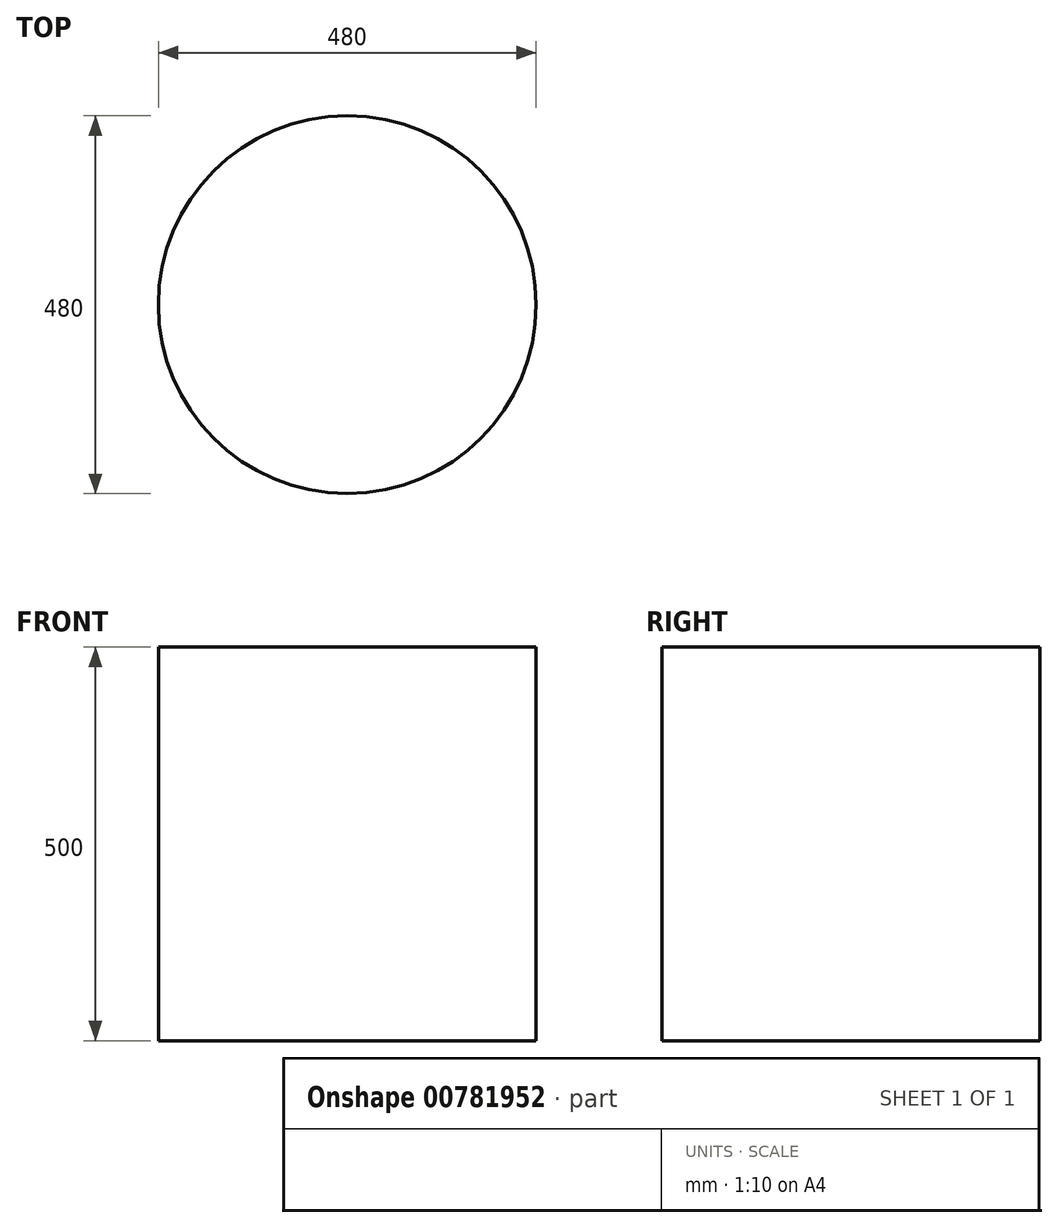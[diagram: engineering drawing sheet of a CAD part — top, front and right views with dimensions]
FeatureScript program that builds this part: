
annotation { "Feature Type Name" : "Feature", "Feature Type Description" : "" }
export const myFeature = defineFeature(function(context is Context, id is Id, definition is map)
    precondition{}
    {
        {
            var Q0;
            Q0=qCreatedBy(makeId("Front.planeOp"),FACE);
            var sketch = newSketch(context, id + "F0", { "sketchPlane" : qUnion([Q0])});
            skLineSegment(sketch, "E0.bottom", {"start": v(0, 479.95) * mm, "end": v(240, 479.95) * mm});
            skLineSegment(sketch, "E0.top", {"start": v(0, -20.05) * mm, "end": v(240, -20.05) * mm});
            skLineSegment(sketch, "E0.left", {"start": v(0, 479.95) * mm, "end": v(0, -20.05) * mm});
            skLineSegment(sketch, "E0.right", {"start": v(240, 479.95) * mm, "end": v(240, -20.05) * mm});
            skSolve(sketch);
        }
        {
            var Q0;
            Q0=makeQuery(id+"F0.imprint","IMPRINT",FACE,{"disambiguationData":[TD([[makeQuery(id+"F0.imprint","IMPRINT",EDGE,{"derivedFrom":sQuery(id+"F0.wireOp",EDGE,"E0.bottom")}),-1.0]])]});
            var Q1;
            Q1=sQuery(id+"F0.wireOp",EDGE,"E0.left");
            revolve(context, id + "F1", {"surfaceOperationType" : NewSurfaceOperationType.NEW, "entities" : qUnion([Q0]), "axis" : qUnion([Q1]), "revolveType" : RevolveType.FULL});
        }
    });
